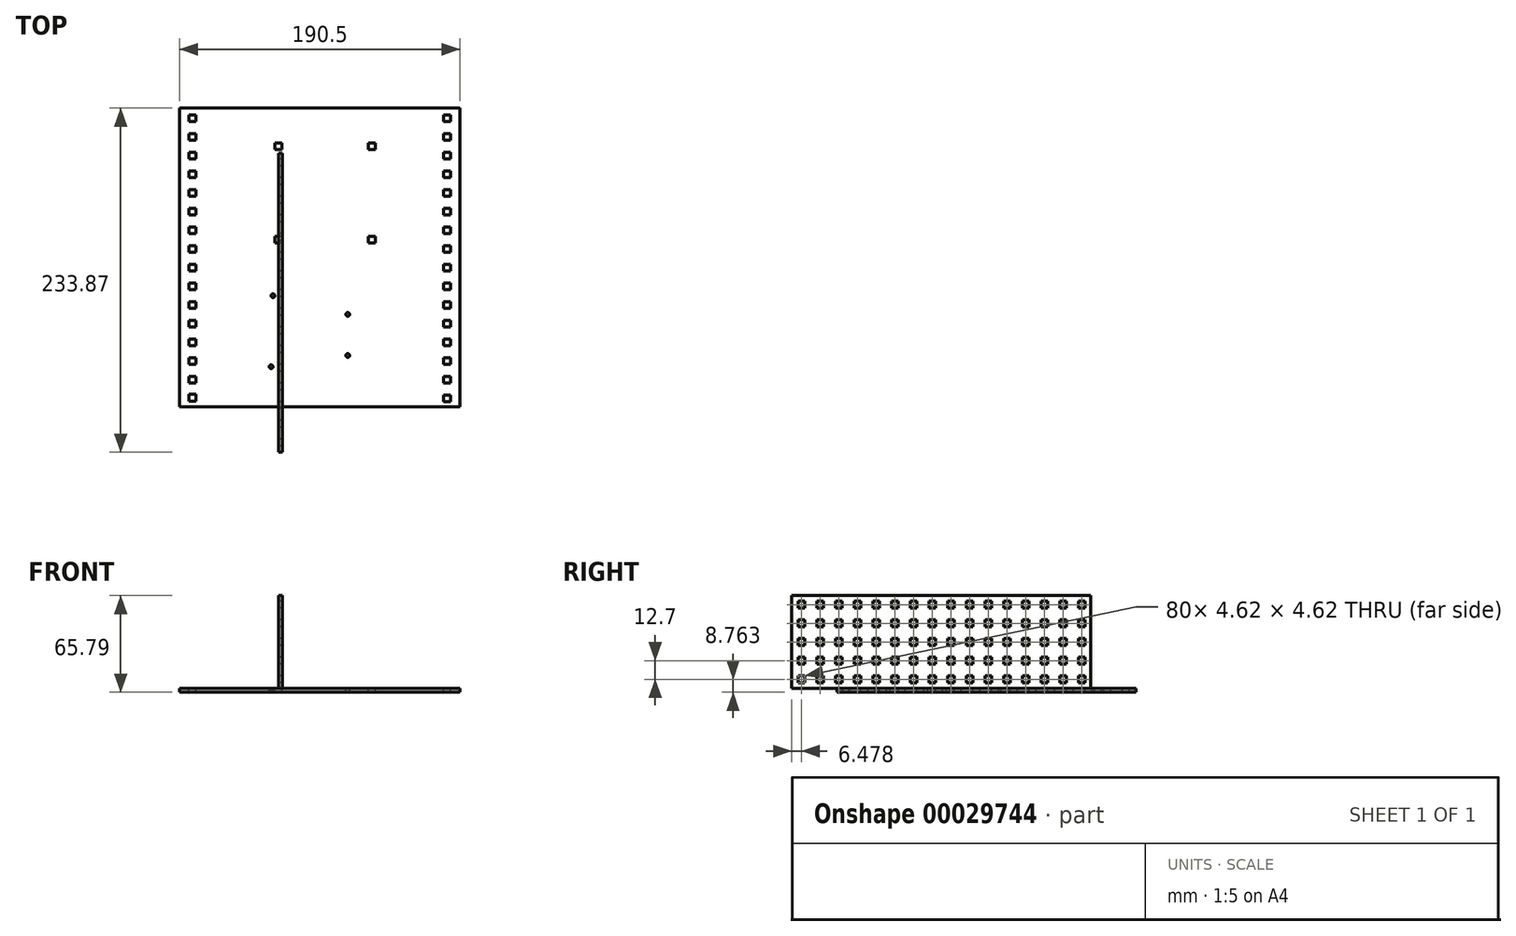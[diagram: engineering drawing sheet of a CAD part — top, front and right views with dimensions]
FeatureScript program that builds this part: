
annotation { "Feature Type Name" : "Feature", "Feature Type Description" : "" }
export const myFeature = defineFeature(function(context is Context, id is Id, definition is map)
    precondition{}
    {
        {
            var Q0;
            Q0=qCreatedBy(makeId("Top.planeOp"),FACE);
            var sketch = newSketch(context, id + "F0", { "sketchPlane" : qUnion([Q0])});
            skLineSegment(sketch, "E0.bottom", {"start": v(116.86, 111.67) * mm, "end": v(112.2, 111.67) * mm});
            skLineSegment(sketch, "E0.top", {"start": v(116.86, 107.05) * mm, "end": v(112.2, 107.05) * mm});
            skLineSegment(sketch, "E0.left", {"start": v(116.86, 111.67) * mm, "end": v(116.86, 107.05) * mm});
            skLineSegment(sketch, "E0.right", {"start": v(112.2, 111.67) * mm, "end": v(112.2, 107.05) * mm});
            skLineSegment(sketch, "E1.0.1.0", {"start": v(116.83, 94.35) * mm, "end": v(112.2, 94.35) * mm});
            skLineSegment(sketch, "E1.0.1.1", {"start": v(116.83, 98.97) * mm, "end": v(116.83, 94.35) * mm});
            skLineSegment(sketch, "E1.0.1.2", {"start": v(112.2, 98.97) * mm, "end": v(112.2, 94.35) * mm});
            skLineSegment(sketch, "E1.0.1.3", {"start": v(116.83, 98.97) * mm, "end": v(112.2, 98.97) * mm});
            skLineSegment(sketch, "E1.0.2.0", {"start": v(116.83, 81.65) * mm, "end": v(112.2, 81.65) * mm});
            skLineSegment(sketch, "E1.0.2.1", {"start": v(116.83, 86.27) * mm, "end": v(116.83, 81.65) * mm});
            skLineSegment(sketch, "E1.0.2.2", {"start": v(112.2, 86.27) * mm, "end": v(112.2, 81.65) * mm});
            skLineSegment(sketch, "E1.0.2.3", {"start": v(116.83, 86.27) * mm, "end": v(112.2, 86.27) * mm});
            skLineSegment(sketch, "E1.0.3.0", {"start": v(116.83, 68.95) * mm, "end": v(112.2, 68.95) * mm});
            skLineSegment(sketch, "E1.0.3.1", {"start": v(116.83, 73.57) * mm, "end": v(116.83, 68.95) * mm});
            skLineSegment(sketch, "E1.0.3.2", {"start": v(112.2, 73.57) * mm, "end": v(112.2, 68.95) * mm});
            skLineSegment(sketch, "E1.0.3.3", {"start": v(116.83, 73.57) * mm, "end": v(112.2, 73.57) * mm});
            skLineSegment(sketch, "E1.0.4.0", {"start": v(116.83, 56.25) * mm, "end": v(112.2, 56.25) * mm});
            skLineSegment(sketch, "E1.0.4.1", {"start": v(116.83, 60.87) * mm, "end": v(116.83, 56.25) * mm});
            skLineSegment(sketch, "E1.0.4.2", {"start": v(112.2, 60.87) * mm, "end": v(112.2, 56.25) * mm});
            skLineSegment(sketch, "E1.0.4.3", {"start": v(116.83, 60.87) * mm, "end": v(112.2, 60.87) * mm});
            skLineSegment(sketch, "E1.0.5.0", {"start": v(116.83, 43.55) * mm, "end": v(112.2, 43.55) * mm});
            skLineSegment(sketch, "E1.0.5.1", {"start": v(116.83, 48.17) * mm, "end": v(116.83, 43.55) * mm});
            skLineSegment(sketch, "E1.0.5.2", {"start": v(112.2, 48.17) * mm, "end": v(112.2, 43.55) * mm});
            skLineSegment(sketch, "E1.0.5.3", {"start": v(116.83, 48.17) * mm, "end": v(112.2, 48.17) * mm});
            skLineSegment(sketch, "E1.0.6.0", {"start": v(116.83, 30.85) * mm, "end": v(112.2, 30.85) * mm});
            skLineSegment(sketch, "E1.0.6.1", {"start": v(116.83, 35.47) * mm, "end": v(116.83, 30.85) * mm});
            skLineSegment(sketch, "E1.0.6.2", {"start": v(112.2, 35.47) * mm, "end": v(112.2, 30.85) * mm});
            skLineSegment(sketch, "E1.0.6.3", {"start": v(116.83, 35.47) * mm, "end": v(112.2, 35.47) * mm});
            skLineSegment(sketch, "E1.0.7.0", {"start": v(116.83, 18.15) * mm, "end": v(112.2, 18.15) * mm});
            skLineSegment(sketch, "E1.0.7.1", {"start": v(116.83, 22.77) * mm, "end": v(116.83, 18.15) * mm});
            skLineSegment(sketch, "E1.0.7.2", {"start": v(112.2, 22.77) * mm, "end": v(112.2, 18.15) * mm});
            skLineSegment(sketch, "E1.0.7.3", {"start": v(116.83, 22.77) * mm, "end": v(112.2, 22.77) * mm});
            skLineSegment(sketch, "E1.0.8.0", {"start": v(116.83, 5.45) * mm, "end": v(112.2, 5.45) * mm});
            skLineSegment(sketch, "E1.0.8.1", {"start": v(116.83, 10.07) * mm, "end": v(116.83, 5.45) * mm});
            skLineSegment(sketch, "E1.0.8.2", {"start": v(112.2, 10.07) * mm, "end": v(112.2, 5.45) * mm});
            skLineSegment(sketch, "E1.0.8.3", {"start": v(116.83, 10.07) * mm, "end": v(112.2, 10.07) * mm});
            skLineSegment(sketch, "E1.0.9.0", {"start": v(116.83, -7.25) * mm, "end": v(112.2, -7.25) * mm});
            skLineSegment(sketch, "E1.0.9.1", {"start": v(116.83, -2.63) * mm, "end": v(116.83, -7.25) * mm});
            skLineSegment(sketch, "E1.0.9.2", {"start": v(112.2, -2.63) * mm, "end": v(112.2, -7.25) * mm});
            skLineSegment(sketch, "E1.0.9.3", {"start": v(116.83, -2.63) * mm, "end": v(112.2, -2.63) * mm});
            skLineSegment(sketch, "E1.0.10.0", {"start": v(116.83, -19.95) * mm, "end": v(112.2, -19.95) * mm});
            skLineSegment(sketch, "E1.0.10.1", {"start": v(116.83, -15.33) * mm, "end": v(116.83, -19.95) * mm});
            skLineSegment(sketch, "E1.0.10.2", {"start": v(112.2, -15.33) * mm, "end": v(112.2, -19.95) * mm});
            skLineSegment(sketch, "E1.0.10.3", {"start": v(116.83, -15.33) * mm, "end": v(112.2, -15.33) * mm});
            skLineSegment(sketch, "E2.bottom", {"start": v(-60.74, 111.67) * mm, "end": v(-56.1, 111.67) * mm});
            skLineSegment(sketch, "E2.top", {"start": v(-60.74, 107.05) * mm, "end": v(-56.1, 107.05) * mm});
            skLineSegment(sketch, "E2.left", {"start": v(-60.74, 111.67) * mm, "end": v(-60.74, 107.05) * mm});
            skLineSegment(sketch, "E2.right", {"start": v(-56.1, 111.67) * mm, "end": v(-56.1, 107.05) * mm});
            skLineSegment(sketch, "E3.0.1.0", {"start": v(-56.1, 98.97) * mm, "end": v(-56.1, 94.35) * mm});
            skLineSegment(sketch, "E3.0.1.1", {"start": v(-60.72, 94.35) * mm, "end": v(-56.1, 94.35) * mm});
            skLineSegment(sketch, "E3.0.1.2", {"start": v(-60.72, 98.97) * mm, "end": v(-60.72, 94.35) * mm});
            skLineSegment(sketch, "E3.0.1.3", {"start": v(-60.72, 98.97) * mm, "end": v(-56.1, 98.97) * mm});
            skLineSegment(sketch, "E3.0.2.0", {"start": v(-56.1, 86.27) * mm, "end": v(-56.1, 81.65) * mm});
            skLineSegment(sketch, "E3.0.2.1", {"start": v(-60.72, 81.65) * mm, "end": v(-56.1, 81.65) * mm});
            skLineSegment(sketch, "E3.0.2.2", {"start": v(-60.72, 86.27) * mm, "end": v(-60.72, 81.65) * mm});
            skLineSegment(sketch, "E3.0.2.3", {"start": v(-60.72, 86.27) * mm, "end": v(-56.1, 86.27) * mm});
            skLineSegment(sketch, "E3.0.3.0", {"start": v(-56.1, 73.57) * mm, "end": v(-56.1, 68.95) * mm});
            skLineSegment(sketch, "E3.0.3.1", {"start": v(-60.72, 68.95) * mm, "end": v(-56.1, 68.95) * mm});
            skLineSegment(sketch, "E3.0.3.2", {"start": v(-60.72, 73.57) * mm, "end": v(-60.72, 68.95) * mm});
            skLineSegment(sketch, "E3.0.3.3", {"start": v(-60.72, 73.57) * mm, "end": v(-56.1, 73.57) * mm});
            skLineSegment(sketch, "E3.0.4.0", {"start": v(-56.1, 60.87) * mm, "end": v(-56.1, 56.25) * mm});
            skLineSegment(sketch, "E3.0.4.1", {"start": v(-60.72, 56.25) * mm, "end": v(-56.1, 56.25) * mm});
            skLineSegment(sketch, "E3.0.4.2", {"start": v(-60.72, 60.87) * mm, "end": v(-60.72, 56.25) * mm});
            skLineSegment(sketch, "E3.0.4.3", {"start": v(-60.72, 60.87) * mm, "end": v(-56.1, 60.87) * mm});
            skLineSegment(sketch, "E3.0.5.0", {"start": v(-56.1, 48.17) * mm, "end": v(-56.1, 43.55) * mm});
            skLineSegment(sketch, "E3.0.5.1", {"start": v(-60.72, 43.55) * mm, "end": v(-56.1, 43.55) * mm});
            skLineSegment(sketch, "E3.0.5.2", {"start": v(-60.72, 48.17) * mm, "end": v(-60.72, 43.55) * mm});
            skLineSegment(sketch, "E3.0.5.3", {"start": v(-60.72, 48.17) * mm, "end": v(-56.1, 48.17) * mm});
            skLineSegment(sketch, "E3.0.6.0", {"start": v(-56.1, 35.47) * mm, "end": v(-56.1, 30.85) * mm});
            skLineSegment(sketch, "E3.0.6.1", {"start": v(-60.72, 30.85) * mm, "end": v(-56.1, 30.85) * mm});
            skLineSegment(sketch, "E3.0.6.2", {"start": v(-60.72, 35.47) * mm, "end": v(-60.72, 30.85) * mm});
            skLineSegment(sketch, "E3.0.6.3", {"start": v(-60.72, 35.47) * mm, "end": v(-56.1, 35.47) * mm});
            skLineSegment(sketch, "E3.0.7.0", {"start": v(-56.1, 22.77) * mm, "end": v(-56.1, 18.15) * mm});
            skLineSegment(sketch, "E3.0.7.1", {"start": v(-60.72, 18.15) * mm, "end": v(-56.1, 18.15) * mm});
            skLineSegment(sketch, "E3.0.7.2", {"start": v(-60.72, 22.77) * mm, "end": v(-60.72, 18.15) * mm});
            skLineSegment(sketch, "E3.0.7.3", {"start": v(-60.72, 22.77) * mm, "end": v(-56.1, 22.77) * mm});
            skLineSegment(sketch, "E3.0.8.0", {"start": v(-56.1, 10.07) * mm, "end": v(-56.1, 5.45) * mm});
            skLineSegment(sketch, "E3.0.8.1", {"start": v(-60.72, 5.45) * mm, "end": v(-56.1, 5.45) * mm});
            skLineSegment(sketch, "E3.0.8.2", {"start": v(-60.72, 10.07) * mm, "end": v(-60.72, 5.45) * mm});
            skLineSegment(sketch, "E3.0.8.3", {"start": v(-60.72, 10.07) * mm, "end": v(-56.1, 10.07) * mm});
            skLineSegment(sketch, "E3.0.9.0", {"start": v(-56.1, -2.63) * mm, "end": v(-56.1, -7.25) * mm});
            skLineSegment(sketch, "E3.0.9.1", {"start": v(-60.72, -7.25) * mm, "end": v(-56.1, -7.25) * mm});
            skLineSegment(sketch, "E3.0.9.2", {"start": v(-60.72, -2.63) * mm, "end": v(-60.72, -7.25) * mm});
            skLineSegment(sketch, "E3.0.9.3", {"start": v(-60.72, -2.63) * mm, "end": v(-56.1, -2.63) * mm});
            skLineSegment(sketch, "E3.0.10.0", {"start": v(-56.1, -15.33) * mm, "end": v(-56.1, -19.95) * mm});
            skLineSegment(sketch, "E3.0.10.1", {"start": v(-60.72, -19.95) * mm, "end": v(-56.1, -19.95) * mm});
            skLineSegment(sketch, "E3.0.10.2", {"start": v(-60.72, -15.33) * mm, "end": v(-60.72, -19.95) * mm});
            skLineSegment(sketch, "E3.0.10.3", {"start": v(-60.72, -15.33) * mm, "end": v(-56.1, -15.33) * mm});
            skLineSegment(sketch, "E4", {"start": v(-67.2, 141.63) * mm, "end": v(-67.2, -61.57) * mm});
            skLineSegment(sketch, "E5.0.0.11", {"start": v(-56.1, -28.03) * mm, "end": v(-56.1, -32.65) * mm});
            skLineSegment(sketch, "E5.3.0.11", {"start": v(-60.72, -32.65) * mm, "end": v(-56.1, -32.65) * mm});
            skLineSegment(sketch, "E5.6.0.11", {"start": v(-60.72, -28.03) * mm, "end": v(-60.72, -32.65) * mm});
            skLineSegment(sketch, "E5.9.0.11", {"start": v(-60.72, -28.03) * mm, "end": v(-56.1, -28.03) * mm});
            skLineSegment(sketch, "E5.0.0.12", {"start": v(-56.1, -40.73) * mm, "end": v(-56.1, -45.35) * mm});
            skLineSegment(sketch, "E5.3.0.12", {"start": v(-60.72, -45.35) * mm, "end": v(-56.1, -45.35) * mm});
            skLineSegment(sketch, "E5.6.0.12", {"start": v(-60.72, -40.73) * mm, "end": v(-60.72, -45.35) * mm});
            skLineSegment(sketch, "E5.9.0.12", {"start": v(-60.72, -40.73) * mm, "end": v(-56.1, -40.73) * mm});
            skLineSegment(sketch, "E5.0.0.13", {"start": v(-56.07, -52.9) * mm, "end": v(-56.07, -57.53) * mm});
            skLineSegment(sketch, "E5.3.0.13", {"start": v(-60.72, -57.53) * mm, "end": v(-56.07, -57.53) * mm});
            skLineSegment(sketch, "E5.6.0.13", {"start": v(-60.72, -52.9) * mm, "end": v(-60.72, -57.53) * mm});
            skLineSegment(sketch, "E5.9.0.13", {"start": v(-60.72, -52.9) * mm, "end": v(-56.07, -52.9) * mm});
            skLineSegment(sketch, "E6.0.0.11", {"start": v(116.83, -32.65) * mm, "end": v(112.2, -32.65) * mm});
            skLineSegment(sketch, "E6.3.0.11", {"start": v(116.83, -28.03) * mm, "end": v(116.83, -32.65) * mm});
            skLineSegment(sketch, "E6.6.0.11", {"start": v(112.2, -28.03) * mm, "end": v(112.2, -32.65) * mm});
            skLineSegment(sketch, "E6.9.0.11", {"start": v(116.83, -28.03) * mm, "end": v(112.2, -28.03) * mm});
            skLineSegment(sketch, "E6.0.0.12", {"start": v(116.83, -45.35) * mm, "end": v(112.2, -45.35) * mm});
            skLineSegment(sketch, "E6.3.0.12", {"start": v(116.83, -40.73) * mm, "end": v(116.83, -45.35) * mm});
            skLineSegment(sketch, "E6.6.0.12", {"start": v(112.2, -40.73) * mm, "end": v(112.2, -45.35) * mm});
            skLineSegment(sketch, "E6.9.0.12", {"start": v(116.83, -40.73) * mm, "end": v(112.2, -40.73) * mm});
            skLineSegment(sketch, "E6.0.0.13", {"start": v(116.83, -58.05) * mm, "end": v(112.2, -58.05) * mm});
            skLineSegment(sketch, "E6.3.0.13", {"start": v(116.83, -53.43) * mm, "end": v(116.83, -58.05) * mm});
            skLineSegment(sketch, "E6.6.0.13", {"start": v(112.2, -53.43) * mm, "end": v(112.2, -58.05) * mm});
            skLineSegment(sketch, "E6.9.0.13", {"start": v(116.83, -53.43) * mm, "end": v(112.2, -53.43) * mm});
            skCircle(sketch, "E7", {"center": v(-3.7, 14.1) * mm, "radius": 1.27 * mm});
            skCircle(sketch, "E8", {"center": v(47.1, 1.4) * mm, "radius": 1.27 * mm});
            skCircle(sketch, "E9", {"center": v(47.1, -26.53) * mm, "radius": 1.27 * mm});
            skCircle(sketch, "E10", {"center": v(-4.96, -34.15) * mm, "radius": 1.27 * mm});
            skLineSegment(sketch, "E11", {"start": v(-60.74, 124.37) * mm, "end": v(-56.1, 124.37) * mm});
            skLineSegment(sketch, "E12", {"start": v(-56.1, 124.37) * mm, "end": v(-56.1, 119.72) * mm});
            skLineSegment(sketch, "E13", {"start": v(-56.1, 119.72) * mm, "end": v(-60.74, 119.72) * mm});
            skLineSegment(sketch, "E14", {"start": v(-56.1, 137.07) * mm, "end": v(-56.1, 132.42) * mm});
            skLineSegment(sketch, "E15", {"start": v(-56.1, 132.42) * mm, "end": v(-60.74, 132.42) * mm});
            skLineSegment(sketch, "E16", {"start": v(-60.74, 124.37) * mm, "end": v(-60.74, 119.72) * mm});
            skLineSegment(sketch, "E17", {"start": v(112.2, 124.37) * mm, "end": v(116.86, 124.37) * mm});
            skLineSegment(sketch, "E18", {"start": v(116.86, 124.37) * mm, "end": v(116.86, 119.72) * mm});
            skLineSegment(sketch, "E19", {"start": v(112.2, 137.07) * mm, "end": v(116.86, 137.07) * mm});
            skLineSegment(sketch, "E20", {"start": v(116.86, 137.07) * mm, "end": v(116.86, 132.42) * mm});
            skLineSegment(sketch, "E21", {"start": v(116.86, 132.42) * mm, "end": v(112.2, 132.42) * mm});
            skLineSegment(sketch, "E22", {"start": v(116.86, 119.72) * mm, "end": v(112.2, 119.72) * mm});
            skLineSegment(sketch, "E23", {"start": v(112.2, 119.72) * mm, "end": v(112.2, 124.37) * mm});
            skLineSegment(sketch, "E24", {"start": v(112.2, 137.07) * mm, "end": v(112.2, 132.42) * mm});
            skLineSegment(sketch, "E25.rect.bottom", {"start": v(2.32, 113.39) * mm, "end": v(-2.32, 113.39) * mm});
            skLineSegment(sketch, "E25.rect.top", {"start": v(2.32, 118.03) * mm, "end": v(-2.32, 118.03) * mm});
            skLineSegment(sketch, "E25.rect.left", {"start": v(2.32, 113.39) * mm, "end": v(2.32, 118.03) * mm});
            skLineSegment(sketch, "E25.rect.right", {"start": v(-2.32, 113.39) * mm, "end": v(-2.32, 118.03) * mm});
            skPoint(sketch, "E25.rect.middle", {"position": v(0, 115.7) * mm});
            skLineSegment(sketch, "E26.rect.bottom", {"start": v(61.18, 113.39) * mm, "end": v(65.82, 113.39) * mm});
            skLineSegment(sketch, "E26.rect.top", {"start": v(61.18, 118.03) * mm, "end": v(65.82, 118.03) * mm});
            skLineSegment(sketch, "E26.rect.left", {"start": v(61.18, 113.39) * mm, "end": v(61.18, 118.03) * mm});
            skLineSegment(sketch, "E26.rect.right", {"start": v(65.82, 113.39) * mm, "end": v(65.82, 118.03) * mm});
            skPoint(sketch, "E26.rect.middle", {"position": v(63.5, 115.7) * mm});
            skPoint(sketch, "E27.endSnap0", {"position": v(0, 113.39) * mm});
            skLineSegment(sketch, "E28.rect.bottom", {"start": v(2.32, 49.89) * mm, "end": v(-2.32, 49.89) * mm});
            skLineSegment(sketch, "E28.rect.top", {"start": v(2.32, 54.53) * mm, "end": v(-2.32, 54.53) * mm});
            skLineSegment(sketch, "E28.rect.left", {"start": v(2.32, 49.89) * mm, "end": v(2.32, 54.53) * mm});
            skLineSegment(sketch, "E28.rect.right", {"start": v(-2.32, 49.89) * mm, "end": v(-2.32, 54.53) * mm});
            skPoint(sketch, "E28.rect.middle", {"position": v(0, 52.2) * mm});
            skLineSegment(sketch, "E29.rect.bottom", {"start": v(65.82, 49.89) * mm, "end": v(61.18, 49.89) * mm});
            skLineSegment(sketch, "E29.rect.top", {"start": v(65.82, 54.53) * mm, "end": v(61.18, 54.53) * mm});
            skLineSegment(sketch, "E29.rect.left", {"start": v(65.82, 49.89) * mm, "end": v(65.82, 54.53) * mm});
            skLineSegment(sketch, "E29.rect.right", {"start": v(61.18, 49.89) * mm, "end": v(61.18, 54.53) * mm});
            skPoint(sketch, "E29.rect.middle", {"position": v(63.5, 52.2) * mm});
            skLineSegment(sketch, "E30", {"start": v(-67.2, -61.57) * mm, "end": v(123.3, -61.57) * mm});
            skLineSegment(sketch, "E31", {"start": v(123.3, 141.63) * mm, "end": v(123.3, -61.57) * mm});
            skLineSegment(sketch, "E32", {"start": v(-67.2, 141.63) * mm, "end": v(123.3, 141.63) * mm});
            skLineSegment(sketch, "E33", {"start": v(-56.1, 137.07) * mm, "end": v(-60.74, 137.07) * mm});
            skLineSegment(sketch, "E34", {"start": v(-60.74, 137.07) * mm, "end": v(-60.74, 132.42) * mm});
            skSolve(sketch);
        }
        {
            var Q0;
            Q0=qCreatedBy(makeId("Right.planeOp"),FACE);
            var sketch = newSketch(context, id + "F1", { "sketchPlane" : qUnion([Q0])});
            skLineSegment(sketch, "E35", {"start": v(110.96, 0) * mm, "end": v(110.96, 63.25) * mm});
            skLineSegment(sketch, "E36", {"start": v(-92.24, 63.25) * mm, "end": v(-92.24, 0) * mm});
            skLineSegment(sketch, "E37", {"start": v(110.96, 63.25) * mm, "end": v(-92.24, 63.25) * mm});
            skLineSegment(sketch, "E38", {"start": v(110.96, 0) * mm, "end": v(-92.24, 0) * mm});
            skLineSegment(sketch, "E39.bottom", {"start": v(107.05, 59.33) * mm, "end": v(102.43, 59.33) * mm});
            skLineSegment(sketch, "E39.top", {"start": v(107.05, 54.71) * mm, "end": v(102.43, 54.71) * mm});
            skLineSegment(sketch, "E39.left", {"start": v(107.05, 59.33) * mm, "end": v(107.05, 54.71) * mm});
            skLineSegment(sketch, "E39.right", {"start": v(102.43, 59.33) * mm, "end": v(102.43, 54.71) * mm});
            skLineSegment(sketch, "E40.0.1.0", {"start": v(107.05, 42.01) * mm, "end": v(102.43, 42.01) * mm});
            skLineSegment(sketch, "E40.0.1.1", {"start": v(107.05, 46.63) * mm, "end": v(107.05, 42.01) * mm});
            skLineSegment(sketch, "E40.0.1.2", {"start": v(107.05, 46.63) * mm, "end": v(102.43, 46.63) * mm});
            skLineSegment(sketch, "E40.0.1.3", {"start": v(102.43, 46.63) * mm, "end": v(102.43, 42.01) * mm});
            skLineSegment(sketch, "E40.0.2.0", {"start": v(107.05, 29.31) * mm, "end": v(102.43, 29.31) * mm});
            skLineSegment(sketch, "E40.0.2.1", {"start": v(107.05, 33.93) * mm, "end": v(107.05, 29.31) * mm});
            skLineSegment(sketch, "E40.0.2.2", {"start": v(107.05, 33.93) * mm, "end": v(102.43, 33.93) * mm});
            skLineSegment(sketch, "E40.0.2.3", {"start": v(102.43, 33.93) * mm, "end": v(102.43, 29.31) * mm});
            skLineSegment(sketch, "E40.0.3.0", {"start": v(107.05, 16.61) * mm, "end": v(102.43, 16.61) * mm});
            skLineSegment(sketch, "E40.0.3.1", {"start": v(107.05, 21.23) * mm, "end": v(107.05, 16.61) * mm});
            skLineSegment(sketch, "E40.0.3.2", {"start": v(107.05, 21.23) * mm, "end": v(102.43, 21.23) * mm});
            skLineSegment(sketch, "E40.0.3.3", {"start": v(102.43, 21.23) * mm, "end": v(102.43, 16.61) * mm});
            skLineSegment(sketch, "E40.0.4.0", {"start": v(107.05, 3.91) * mm, "end": v(102.43, 3.91) * mm});
            skLineSegment(sketch, "E40.0.4.1", {"start": v(107.05, 8.53) * mm, "end": v(107.05, 3.91) * mm});
            skLineSegment(sketch, "E40.0.4.2", {"start": v(107.05, 8.53) * mm, "end": v(102.43, 8.53) * mm});
            skLineSegment(sketch, "E40.0.4.3", {"start": v(102.43, 8.53) * mm, "end": v(102.43, 3.91) * mm});
            skLineSegment(sketch, "E40.1.0.0", {"start": v(94.35, 54.71) * mm, "end": v(89.73, 54.71) * mm});
            skLineSegment(sketch, "E40.1.0.1", {"start": v(94.35, 59.33) * mm, "end": v(94.35, 54.71) * mm});
            skLineSegment(sketch, "E40.1.0.2", {"start": v(94.35, 59.33) * mm, "end": v(89.73, 59.33) * mm});
            skLineSegment(sketch, "E40.1.0.3", {"start": v(89.73, 59.33) * mm, "end": v(89.73, 54.71) * mm});
            skLineSegment(sketch, "E40.1.1.0", {"start": v(94.35, 42.01) * mm, "end": v(89.73, 42.01) * mm});
            skLineSegment(sketch, "E40.1.1.1", {"start": v(94.35, 46.63) * mm, "end": v(94.35, 42.01) * mm});
            skLineSegment(sketch, "E40.1.1.2", {"start": v(94.35, 46.63) * mm, "end": v(89.73, 46.63) * mm});
            skLineSegment(sketch, "E40.1.1.3", {"start": v(89.73, 46.63) * mm, "end": v(89.73, 42.01) * mm});
            skLineSegment(sketch, "E40.1.2.0", {"start": v(94.35, 29.31) * mm, "end": v(89.73, 29.31) * mm});
            skLineSegment(sketch, "E40.1.2.1", {"start": v(94.35, 33.93) * mm, "end": v(94.35, 29.31) * mm});
            skLineSegment(sketch, "E40.1.2.2", {"start": v(94.35, 33.93) * mm, "end": v(89.73, 33.93) * mm});
            skLineSegment(sketch, "E40.1.2.3", {"start": v(89.73, 33.93) * mm, "end": v(89.73, 29.31) * mm});
            skLineSegment(sketch, "E40.1.3.0", {"start": v(94.35, 16.61) * mm, "end": v(89.73, 16.61) * mm});
            skLineSegment(sketch, "E40.1.3.1", {"start": v(94.35, 21.23) * mm, "end": v(94.35, 16.61) * mm});
            skLineSegment(sketch, "E40.1.3.2", {"start": v(94.35, 21.23) * mm, "end": v(89.73, 21.23) * mm});
            skLineSegment(sketch, "E40.1.3.3", {"start": v(89.73, 21.23) * mm, "end": v(89.73, 16.61) * mm});
            skLineSegment(sketch, "E40.1.4.0", {"start": v(94.35, 3.91) * mm, "end": v(89.73, 3.91) * mm});
            skLineSegment(sketch, "E40.1.4.1", {"start": v(94.35, 8.53) * mm, "end": v(94.35, 3.91) * mm});
            skLineSegment(sketch, "E40.1.4.2", {"start": v(94.35, 8.53) * mm, "end": v(89.73, 8.53) * mm});
            skLineSegment(sketch, "E40.1.4.3", {"start": v(89.73, 8.53) * mm, "end": v(89.73, 3.91) * mm});
            skLineSegment(sketch, "E40.2.0.0", {"start": v(81.65, 54.71) * mm, "end": v(77.03, 54.71) * mm});
            skLineSegment(sketch, "E40.2.0.1", {"start": v(81.65, 59.33) * mm, "end": v(81.65, 54.71) * mm});
            skLineSegment(sketch, "E40.2.0.2", {"start": v(81.65, 59.33) * mm, "end": v(77.03, 59.33) * mm});
            skLineSegment(sketch, "E40.2.0.3", {"start": v(77.03, 59.33) * mm, "end": v(77.03, 54.71) * mm});
            skLineSegment(sketch, "E40.2.1.0", {"start": v(81.65, 42.01) * mm, "end": v(77.03, 42.01) * mm});
            skLineSegment(sketch, "E40.2.1.1", {"start": v(81.65, 46.63) * mm, "end": v(81.65, 42.01) * mm});
            skLineSegment(sketch, "E40.2.1.2", {"start": v(81.65, 46.63) * mm, "end": v(77.03, 46.63) * mm});
            skLineSegment(sketch, "E40.2.1.3", {"start": v(77.03, 46.63) * mm, "end": v(77.03, 42.01) * mm});
            skLineSegment(sketch, "E40.2.2.0", {"start": v(81.65, 29.31) * mm, "end": v(77.03, 29.31) * mm});
            skLineSegment(sketch, "E40.2.2.1", {"start": v(81.65, 33.93) * mm, "end": v(81.65, 29.31) * mm});
            skLineSegment(sketch, "E40.2.2.2", {"start": v(81.65, 33.93) * mm, "end": v(77.03, 33.93) * mm});
            skLineSegment(sketch, "E40.2.2.3", {"start": v(77.03, 33.93) * mm, "end": v(77.03, 29.31) * mm});
            skLineSegment(sketch, "E40.2.3.0", {"start": v(81.65, 16.61) * mm, "end": v(77.03, 16.61) * mm});
            skLineSegment(sketch, "E40.2.3.1", {"start": v(81.65, 21.23) * mm, "end": v(81.65, 16.61) * mm});
            skLineSegment(sketch, "E40.2.3.2", {"start": v(81.65, 21.23) * mm, "end": v(77.03, 21.23) * mm});
            skLineSegment(sketch, "E40.2.3.3", {"start": v(77.03, 21.23) * mm, "end": v(77.03, 16.61) * mm});
            skLineSegment(sketch, "E40.2.4.0", {"start": v(81.65, 3.91) * mm, "end": v(77.03, 3.91) * mm});
            skLineSegment(sketch, "E40.2.4.1", {"start": v(81.65, 8.53) * mm, "end": v(81.65, 3.91) * mm});
            skLineSegment(sketch, "E40.2.4.2", {"start": v(81.65, 8.53) * mm, "end": v(77.03, 8.53) * mm});
            skLineSegment(sketch, "E40.2.4.3", {"start": v(77.03, 8.53) * mm, "end": v(77.03, 3.91) * mm});
            skLineSegment(sketch, "E40.3.0.0", {"start": v(68.95, 54.71) * mm, "end": v(64.33, 54.71) * mm});
            skLineSegment(sketch, "E40.3.0.1", {"start": v(68.95, 59.33) * mm, "end": v(68.95, 54.71) * mm});
            skLineSegment(sketch, "E40.3.0.2", {"start": v(68.95, 59.33) * mm, "end": v(64.33, 59.33) * mm});
            skLineSegment(sketch, "E40.3.0.3", {"start": v(64.33, 59.33) * mm, "end": v(64.33, 54.71) * mm});
            skLineSegment(sketch, "E40.3.1.0", {"start": v(68.95, 42.01) * mm, "end": v(64.33, 42.01) * mm});
            skLineSegment(sketch, "E40.3.1.1", {"start": v(68.95, 46.63) * mm, "end": v(68.95, 42.01) * mm});
            skLineSegment(sketch, "E40.3.1.2", {"start": v(68.95, 46.63) * mm, "end": v(64.33, 46.63) * mm});
            skLineSegment(sketch, "E40.3.1.3", {"start": v(64.33, 46.63) * mm, "end": v(64.33, 42.01) * mm});
            skLineSegment(sketch, "E40.3.2.0", {"start": v(68.95, 29.31) * mm, "end": v(64.33, 29.31) * mm});
            skLineSegment(sketch, "E40.3.2.1", {"start": v(68.95, 33.93) * mm, "end": v(68.95, 29.31) * mm});
            skLineSegment(sketch, "E40.3.2.2", {"start": v(68.95, 33.93) * mm, "end": v(64.33, 33.93) * mm});
            skLineSegment(sketch, "E40.3.2.3", {"start": v(64.33, 33.93) * mm, "end": v(64.33, 29.31) * mm});
            skLineSegment(sketch, "E40.3.3.0", {"start": v(68.95, 16.61) * mm, "end": v(64.33, 16.61) * mm});
            skLineSegment(sketch, "E40.3.3.1", {"start": v(68.95, 21.23) * mm, "end": v(68.95, 16.61) * mm});
            skLineSegment(sketch, "E40.3.3.2", {"start": v(68.95, 21.23) * mm, "end": v(64.33, 21.23) * mm});
            skLineSegment(sketch, "E40.3.3.3", {"start": v(64.33, 21.23) * mm, "end": v(64.33, 16.61) * mm});
            skLineSegment(sketch, "E40.3.4.0", {"start": v(68.95, 3.91) * mm, "end": v(64.33, 3.91) * mm});
            skLineSegment(sketch, "E40.3.4.1", {"start": v(68.95, 8.53) * mm, "end": v(68.95, 3.91) * mm});
            skLineSegment(sketch, "E40.3.4.2", {"start": v(68.95, 8.53) * mm, "end": v(64.33, 8.53) * mm});
            skLineSegment(sketch, "E40.3.4.3", {"start": v(64.33, 8.53) * mm, "end": v(64.33, 3.91) * mm});
            skLineSegment(sketch, "E40.4.0.0", {"start": v(56.25, 54.71) * mm, "end": v(51.63, 54.71) * mm});
            skLineSegment(sketch, "E40.4.0.1", {"start": v(56.25, 59.33) * mm, "end": v(56.25, 54.71) * mm});
            skLineSegment(sketch, "E40.4.0.2", {"start": v(56.25, 59.33) * mm, "end": v(51.63, 59.33) * mm});
            skLineSegment(sketch, "E40.4.0.3", {"start": v(51.63, 59.33) * mm, "end": v(51.63, 54.71) * mm});
            skLineSegment(sketch, "E40.4.1.0", {"start": v(56.25, 42.01) * mm, "end": v(51.63, 42.01) * mm});
            skLineSegment(sketch, "E40.4.1.1", {"start": v(56.25, 46.63) * mm, "end": v(56.25, 42.01) * mm});
            skLineSegment(sketch, "E40.4.1.2", {"start": v(56.25, 46.63) * mm, "end": v(51.63, 46.63) * mm});
            skLineSegment(sketch, "E40.4.1.3", {"start": v(51.63, 46.63) * mm, "end": v(51.63, 42.01) * mm});
            skLineSegment(sketch, "E40.4.2.0", {"start": v(56.25, 29.31) * mm, "end": v(51.63, 29.31) * mm});
            skLineSegment(sketch, "E40.4.2.1", {"start": v(56.25, 33.93) * mm, "end": v(56.25, 29.31) * mm});
            skLineSegment(sketch, "E40.4.2.2", {"start": v(56.25, 33.93) * mm, "end": v(51.63, 33.93) * mm});
            skLineSegment(sketch, "E40.4.2.3", {"start": v(51.63, 33.93) * mm, "end": v(51.63, 29.31) * mm});
            skLineSegment(sketch, "E40.4.3.0", {"start": v(56.25, 16.61) * mm, "end": v(51.63, 16.61) * mm});
            skLineSegment(sketch, "E40.4.3.1", {"start": v(56.25, 21.23) * mm, "end": v(56.25, 16.61) * mm});
            skLineSegment(sketch, "E40.4.3.2", {"start": v(56.25, 21.23) * mm, "end": v(51.63, 21.23) * mm});
            skLineSegment(sketch, "E40.4.3.3", {"start": v(51.63, 21.23) * mm, "end": v(51.63, 16.61) * mm});
            skLineSegment(sketch, "E40.4.4.0", {"start": v(56.25, 3.91) * mm, "end": v(51.63, 3.91) * mm});
            skLineSegment(sketch, "E40.4.4.1", {"start": v(56.25, 8.53) * mm, "end": v(56.25, 3.91) * mm});
            skLineSegment(sketch, "E40.4.4.2", {"start": v(56.25, 8.53) * mm, "end": v(51.63, 8.53) * mm});
            skLineSegment(sketch, "E40.4.4.3", {"start": v(51.63, 8.53) * mm, "end": v(51.63, 3.91) * mm});
            skLineSegment(sketch, "E40.5.0.0", {"start": v(43.55, 54.71) * mm, "end": v(38.93, 54.71) * mm});
            skLineSegment(sketch, "E40.5.0.1", {"start": v(43.55, 59.33) * mm, "end": v(43.55, 54.71) * mm});
            skLineSegment(sketch, "E40.5.0.2", {"start": v(43.55, 59.33) * mm, "end": v(38.93, 59.33) * mm});
            skLineSegment(sketch, "E40.5.0.3", {"start": v(38.93, 59.33) * mm, "end": v(38.93, 54.71) * mm});
            skLineSegment(sketch, "E40.5.1.0", {"start": v(43.55, 42.01) * mm, "end": v(38.93, 42.01) * mm});
            skLineSegment(sketch, "E40.5.1.1", {"start": v(43.55, 46.63) * mm, "end": v(43.55, 42.01) * mm});
            skLineSegment(sketch, "E40.5.1.2", {"start": v(43.55, 46.63) * mm, "end": v(38.93, 46.63) * mm});
            skLineSegment(sketch, "E40.5.1.3", {"start": v(38.93, 46.63) * mm, "end": v(38.93, 42.01) * mm});
            skLineSegment(sketch, "E40.5.2.0", {"start": v(43.55, 29.31) * mm, "end": v(38.93, 29.31) * mm});
            skLineSegment(sketch, "E40.5.2.1", {"start": v(43.55, 33.93) * mm, "end": v(43.55, 29.31) * mm});
            skLineSegment(sketch, "E40.5.2.2", {"start": v(43.55, 33.93) * mm, "end": v(38.93, 33.93) * mm});
            skLineSegment(sketch, "E40.5.2.3", {"start": v(38.93, 33.93) * mm, "end": v(38.93, 29.31) * mm});
            skLineSegment(sketch, "E40.5.3.0", {"start": v(43.55, 16.61) * mm, "end": v(38.93, 16.61) * mm});
            skLineSegment(sketch, "E40.5.3.1", {"start": v(43.55, 21.23) * mm, "end": v(43.55, 16.61) * mm});
            skLineSegment(sketch, "E40.5.3.2", {"start": v(43.55, 21.23) * mm, "end": v(38.93, 21.23) * mm});
            skLineSegment(sketch, "E40.5.3.3", {"start": v(38.93, 21.23) * mm, "end": v(38.93, 16.61) * mm});
            skLineSegment(sketch, "E40.5.4.0", {"start": v(43.55, 3.91) * mm, "end": v(38.93, 3.91) * mm});
            skLineSegment(sketch, "E40.5.4.1", {"start": v(43.55, 8.53) * mm, "end": v(43.55, 3.91) * mm});
            skLineSegment(sketch, "E40.5.4.2", {"start": v(43.55, 8.53) * mm, "end": v(38.93, 8.53) * mm});
            skLineSegment(sketch, "E40.5.4.3", {"start": v(38.93, 8.53) * mm, "end": v(38.93, 3.91) * mm});
            skLineSegment(sketch, "E40.6.0.0", {"start": v(30.85, 54.71) * mm, "end": v(26.23, 54.71) * mm});
            skLineSegment(sketch, "E40.6.0.1", {"start": v(30.85, 59.33) * mm, "end": v(30.85, 54.71) * mm});
            skLineSegment(sketch, "E40.6.0.2", {"start": v(30.85, 59.33) * mm, "end": v(26.23, 59.33) * mm});
            skLineSegment(sketch, "E40.6.0.3", {"start": v(26.23, 59.33) * mm, "end": v(26.23, 54.71) * mm});
            skLineSegment(sketch, "E40.6.1.0", {"start": v(30.85, 42.01) * mm, "end": v(26.23, 42.01) * mm});
            skLineSegment(sketch, "E40.6.1.1", {"start": v(30.85, 46.63) * mm, "end": v(30.85, 42.01) * mm});
            skLineSegment(sketch, "E40.6.1.2", {"start": v(30.85, 46.63) * mm, "end": v(26.23, 46.63) * mm});
            skLineSegment(sketch, "E40.6.1.3", {"start": v(26.23, 46.63) * mm, "end": v(26.23, 42.01) * mm});
            skLineSegment(sketch, "E40.6.2.0", {"start": v(30.85, 29.31) * mm, "end": v(26.23, 29.31) * mm});
            skLineSegment(sketch, "E40.6.2.1", {"start": v(30.85, 33.93) * mm, "end": v(30.85, 29.31) * mm});
            skLineSegment(sketch, "E40.6.2.2", {"start": v(30.85, 33.93) * mm, "end": v(26.23, 33.93) * mm});
            skLineSegment(sketch, "E40.6.2.3", {"start": v(26.23, 33.93) * mm, "end": v(26.23, 29.31) * mm});
            skLineSegment(sketch, "E40.6.3.0", {"start": v(30.85, 16.61) * mm, "end": v(26.23, 16.61) * mm});
            skLineSegment(sketch, "E40.6.3.1", {"start": v(30.85, 21.23) * mm, "end": v(30.85, 16.61) * mm});
            skLineSegment(sketch, "E40.6.3.2", {"start": v(30.85, 21.23) * mm, "end": v(26.23, 21.23) * mm});
            skLineSegment(sketch, "E40.6.3.3", {"start": v(26.23, 21.23) * mm, "end": v(26.23, 16.61) * mm});
            skLineSegment(sketch, "E40.6.4.0", {"start": v(30.85, 3.91) * mm, "end": v(26.23, 3.91) * mm});
            skLineSegment(sketch, "E40.6.4.1", {"start": v(30.85, 8.53) * mm, "end": v(30.85, 3.91) * mm});
            skLineSegment(sketch, "E40.6.4.2", {"start": v(30.85, 8.53) * mm, "end": v(26.23, 8.53) * mm});
            skLineSegment(sketch, "E40.6.4.3", {"start": v(26.23, 8.53) * mm, "end": v(26.23, 3.91) * mm});
            skLineSegment(sketch, "E40.7.0.0", {"start": v(18.15, 54.71) * mm, "end": v(13.53, 54.71) * mm});
            skLineSegment(sketch, "E40.7.0.1", {"start": v(18.15, 59.33) * mm, "end": v(18.15, 54.71) * mm});
            skLineSegment(sketch, "E40.7.0.2", {"start": v(18.15, 59.33) * mm, "end": v(13.53, 59.33) * mm});
            skLineSegment(sketch, "E40.7.0.3", {"start": v(13.53, 59.33) * mm, "end": v(13.53, 54.71) * mm});
            skLineSegment(sketch, "E40.7.1.0", {"start": v(18.15, 42.01) * mm, "end": v(13.53, 42.01) * mm});
            skLineSegment(sketch, "E40.7.1.1", {"start": v(18.15, 46.63) * mm, "end": v(18.15, 42.01) * mm});
            skLineSegment(sketch, "E40.7.1.2", {"start": v(18.15, 46.63) * mm, "end": v(13.53, 46.63) * mm});
            skLineSegment(sketch, "E40.7.1.3", {"start": v(13.53, 46.63) * mm, "end": v(13.53, 42.01) * mm});
            skLineSegment(sketch, "E40.7.2.0", {"start": v(18.15, 29.31) * mm, "end": v(13.53, 29.31) * mm});
            skLineSegment(sketch, "E40.7.2.1", {"start": v(18.15, 33.93) * mm, "end": v(18.15, 29.31) * mm});
            skLineSegment(sketch, "E40.7.2.2", {"start": v(18.15, 33.93) * mm, "end": v(13.53, 33.93) * mm});
            skLineSegment(sketch, "E40.7.2.3", {"start": v(13.53, 33.93) * mm, "end": v(13.53, 29.31) * mm});
            skLineSegment(sketch, "E40.7.3.0", {"start": v(18.15, 16.61) * mm, "end": v(13.53, 16.61) * mm});
            skLineSegment(sketch, "E40.7.3.1", {"start": v(18.15, 21.23) * mm, "end": v(18.15, 16.61) * mm});
            skLineSegment(sketch, "E40.7.3.2", {"start": v(18.15, 21.23) * mm, "end": v(13.53, 21.23) * mm});
            skLineSegment(sketch, "E40.7.3.3", {"start": v(13.53, 21.23) * mm, "end": v(13.53, 16.61) * mm});
            skLineSegment(sketch, "E40.7.4.0", {"start": v(18.15, 3.91) * mm, "end": v(13.53, 3.91) * mm});
            skLineSegment(sketch, "E40.7.4.1", {"start": v(18.15, 8.53) * mm, "end": v(18.15, 3.91) * mm});
            skLineSegment(sketch, "E40.7.4.2", {"start": v(18.15, 8.53) * mm, "end": v(13.53, 8.53) * mm});
            skLineSegment(sketch, "E40.7.4.3", {"start": v(13.53, 8.53) * mm, "end": v(13.53, 3.91) * mm});
            skLineSegment(sketch, "E40.8.0.0", {"start": v(5.45, 54.71) * mm, "end": v(0.83, 54.71) * mm});
            skLineSegment(sketch, "E40.8.0.1", {"start": v(5.45, 59.33) * mm, "end": v(5.45, 54.71) * mm});
            skLineSegment(sketch, "E40.8.0.2", {"start": v(5.45, 59.33) * mm, "end": v(0.83, 59.33) * mm});
            skLineSegment(sketch, "E40.8.0.3", {"start": v(0.83, 59.33) * mm, "end": v(0.83, 54.71) * mm});
            skLineSegment(sketch, "E40.8.1.0", {"start": v(5.45, 42.01) * mm, "end": v(0.83, 42.01) * mm});
            skLineSegment(sketch, "E40.8.1.1", {"start": v(5.45, 46.63) * mm, "end": v(5.45, 42.01) * mm});
            skLineSegment(sketch, "E40.8.1.2", {"start": v(5.45, 46.63) * mm, "end": v(0.83, 46.63) * mm});
            skLineSegment(sketch, "E40.8.1.3", {"start": v(0.83, 46.63) * mm, "end": v(0.83, 42.01) * mm});
            skLineSegment(sketch, "E40.8.2.0", {"start": v(5.45, 29.31) * mm, "end": v(0.83, 29.31) * mm});
            skLineSegment(sketch, "E40.8.2.1", {"start": v(5.45, 33.93) * mm, "end": v(5.45, 29.31) * mm});
            skLineSegment(sketch, "E40.8.2.2", {"start": v(5.45, 33.93) * mm, "end": v(0.83, 33.93) * mm});
            skLineSegment(sketch, "E40.8.2.3", {"start": v(0.83, 33.93) * mm, "end": v(0.83, 29.31) * mm});
            skLineSegment(sketch, "E40.8.3.0", {"start": v(5.45, 16.61) * mm, "end": v(0.83, 16.61) * mm});
            skLineSegment(sketch, "E40.8.3.1", {"start": v(5.45, 21.23) * mm, "end": v(5.45, 16.61) * mm});
            skLineSegment(sketch, "E40.8.3.2", {"start": v(5.45, 21.23) * mm, "end": v(0.83, 21.23) * mm});
            skLineSegment(sketch, "E40.8.3.3", {"start": v(0.83, 21.23) * mm, "end": v(0.83, 16.61) * mm});
            skLineSegment(sketch, "E40.8.4.0", {"start": v(5.45, 3.91) * mm, "end": v(0.83, 3.91) * mm});
            skLineSegment(sketch, "E40.8.4.1", {"start": v(5.45, 8.53) * mm, "end": v(5.45, 3.91) * mm});
            skLineSegment(sketch, "E40.8.4.2", {"start": v(5.45, 8.53) * mm, "end": v(0.83, 8.53) * mm});
            skLineSegment(sketch, "E40.8.4.3", {"start": v(0.83, 8.53) * mm, "end": v(0.83, 3.91) * mm});
            skLineSegment(sketch, "E40.9.0.0", {"start": v(-7.25, 54.71) * mm, "end": v(-11.87, 54.71) * mm});
            skLineSegment(sketch, "E40.9.0.1", {"start": v(-7.25, 59.33) * mm, "end": v(-7.25, 54.71) * mm});
            skLineSegment(sketch, "E40.9.0.2", {"start": v(-7.25, 59.33) * mm, "end": v(-11.87, 59.33) * mm});
            skLineSegment(sketch, "E40.9.0.3", {"start": v(-11.87, 59.33) * mm, "end": v(-11.87, 54.71) * mm});
            skLineSegment(sketch, "E40.9.1.0", {"start": v(-7.25, 42.01) * mm, "end": v(-11.87, 42.01) * mm});
            skLineSegment(sketch, "E40.9.1.1", {"start": v(-7.25, 46.63) * mm, "end": v(-7.25, 42.01) * mm});
            skLineSegment(sketch, "E40.9.1.2", {"start": v(-7.25, 46.63) * mm, "end": v(-11.87, 46.63) * mm});
            skLineSegment(sketch, "E40.9.1.3", {"start": v(-11.87, 46.63) * mm, "end": v(-11.87, 42.01) * mm});
            skLineSegment(sketch, "E40.9.2.0", {"start": v(-7.25, 29.31) * mm, "end": v(-11.87, 29.31) * mm});
            skLineSegment(sketch, "E40.9.2.1", {"start": v(-7.25, 33.93) * mm, "end": v(-7.25, 29.31) * mm});
            skLineSegment(sketch, "E40.9.2.2", {"start": v(-7.25, 33.93) * mm, "end": v(-11.87, 33.93) * mm});
            skLineSegment(sketch, "E40.9.2.3", {"start": v(-11.87, 33.93) * mm, "end": v(-11.87, 29.31) * mm});
            skLineSegment(sketch, "E40.9.3.0", {"start": v(-7.25, 16.61) * mm, "end": v(-11.87, 16.61) * mm});
            skLineSegment(sketch, "E40.9.3.1", {"start": v(-7.25, 21.23) * mm, "end": v(-7.25, 16.61) * mm});
            skLineSegment(sketch, "E40.9.3.2", {"start": v(-7.25, 21.23) * mm, "end": v(-11.87, 21.23) * mm});
            skLineSegment(sketch, "E40.9.3.3", {"start": v(-11.87, 21.23) * mm, "end": v(-11.87, 16.61) * mm});
            skLineSegment(sketch, "E40.9.4.0", {"start": v(-7.25, 3.91) * mm, "end": v(-11.87, 3.91) * mm});
            skLineSegment(sketch, "E40.9.4.1", {"start": v(-7.25, 8.53) * mm, "end": v(-7.25, 3.91) * mm});
            skLineSegment(sketch, "E40.9.4.2", {"start": v(-7.25, 8.53) * mm, "end": v(-11.87, 8.53) * mm});
            skLineSegment(sketch, "E40.9.4.3", {"start": v(-11.87, 8.53) * mm, "end": v(-11.87, 3.91) * mm});
            skLineSegment(sketch, "E40.10.0.0", {"start": v(-19.95, 54.71) * mm, "end": v(-24.57, 54.71) * mm});
            skLineSegment(sketch, "E40.10.0.1", {"start": v(-19.95, 59.33) * mm, "end": v(-19.95, 54.71) * mm});
            skLineSegment(sketch, "E40.10.0.2", {"start": v(-19.95, 59.33) * mm, "end": v(-24.57, 59.33) * mm});
            skLineSegment(sketch, "E40.10.0.3", {"start": v(-24.57, 59.33) * mm, "end": v(-24.57, 54.71) * mm});
            skLineSegment(sketch, "E40.10.1.0", {"start": v(-19.95, 42.01) * mm, "end": v(-24.57, 42.01) * mm});
            skLineSegment(sketch, "E40.10.1.1", {"start": v(-19.95, 46.63) * mm, "end": v(-19.95, 42.01) * mm});
            skLineSegment(sketch, "E40.10.1.2", {"start": v(-19.95, 46.63) * mm, "end": v(-24.57, 46.63) * mm});
            skLineSegment(sketch, "E40.10.1.3", {"start": v(-24.57, 46.63) * mm, "end": v(-24.57, 42.01) * mm});
            skLineSegment(sketch, "E40.10.2.0", {"start": v(-19.95, 29.31) * mm, "end": v(-24.57, 29.31) * mm});
            skLineSegment(sketch, "E40.10.2.1", {"start": v(-19.95, 33.93) * mm, "end": v(-19.95, 29.31) * mm});
            skLineSegment(sketch, "E40.10.2.2", {"start": v(-19.95, 33.93) * mm, "end": v(-24.57, 33.93) * mm});
            skLineSegment(sketch, "E40.10.2.3", {"start": v(-24.57, 33.93) * mm, "end": v(-24.57, 29.31) * mm});
            skLineSegment(sketch, "E40.10.3.0", {"start": v(-19.95, 16.61) * mm, "end": v(-24.57, 16.61) * mm});
            skLineSegment(sketch, "E40.10.3.1", {"start": v(-19.95, 21.23) * mm, "end": v(-19.95, 16.61) * mm});
            skLineSegment(sketch, "E40.10.3.2", {"start": v(-19.95, 21.23) * mm, "end": v(-24.57, 21.23) * mm});
            skLineSegment(sketch, "E40.10.3.3", {"start": v(-24.57, 21.23) * mm, "end": v(-24.57, 16.61) * mm});
            skLineSegment(sketch, "E40.10.4.0", {"start": v(-19.95, 3.91) * mm, "end": v(-24.57, 3.91) * mm});
            skLineSegment(sketch, "E40.10.4.1", {"start": v(-19.95, 8.53) * mm, "end": v(-19.95, 3.91) * mm});
            skLineSegment(sketch, "E40.10.4.2", {"start": v(-19.95, 8.53) * mm, "end": v(-24.57, 8.53) * mm});
            skLineSegment(sketch, "E40.10.4.3", {"start": v(-24.57, 8.53) * mm, "end": v(-24.57, 3.91) * mm});
            skLineSegment(sketch, "E40.11.0.0", {"start": v(-32.65, 54.71) * mm, "end": v(-37.27, 54.71) * mm});
            skLineSegment(sketch, "E40.11.0.1", {"start": v(-32.65, 59.33) * mm, "end": v(-32.65, 54.71) * mm});
            skLineSegment(sketch, "E40.11.0.2", {"start": v(-32.65, 59.33) * mm, "end": v(-37.27, 59.33) * mm});
            skLineSegment(sketch, "E40.11.0.3", {"start": v(-37.27, 59.33) * mm, "end": v(-37.27, 54.71) * mm});
            skLineSegment(sketch, "E40.11.1.0", {"start": v(-32.65, 42.01) * mm, "end": v(-37.27, 42.01) * mm});
            skLineSegment(sketch, "E40.11.1.1", {"start": v(-32.65, 46.63) * mm, "end": v(-32.65, 42.01) * mm});
            skLineSegment(sketch, "E40.11.1.2", {"start": v(-32.65, 46.63) * mm, "end": v(-37.27, 46.63) * mm});
            skLineSegment(sketch, "E40.11.1.3", {"start": v(-37.27, 46.63) * mm, "end": v(-37.27, 42.01) * mm});
            skLineSegment(sketch, "E40.11.2.0", {"start": v(-32.65, 29.31) * mm, "end": v(-37.27, 29.31) * mm});
            skLineSegment(sketch, "E40.11.2.1", {"start": v(-32.65, 33.93) * mm, "end": v(-32.65, 29.31) * mm});
            skLineSegment(sketch, "E40.11.2.2", {"start": v(-32.65, 33.93) * mm, "end": v(-37.27, 33.93) * mm});
            skLineSegment(sketch, "E40.11.2.3", {"start": v(-37.27, 33.93) * mm, "end": v(-37.27, 29.31) * mm});
            skLineSegment(sketch, "E40.11.3.0", {"start": v(-32.65, 16.61) * mm, "end": v(-37.27, 16.61) * mm});
            skLineSegment(sketch, "E40.11.3.1", {"start": v(-32.65, 21.23) * mm, "end": v(-32.65, 16.61) * mm});
            skLineSegment(sketch, "E40.11.3.2", {"start": v(-32.65, 21.23) * mm, "end": v(-37.27, 21.23) * mm});
            skLineSegment(sketch, "E40.11.3.3", {"start": v(-37.27, 21.23) * mm, "end": v(-37.27, 16.61) * mm});
            skLineSegment(sketch, "E40.11.4.0", {"start": v(-32.65, 3.91) * mm, "end": v(-37.27, 3.91) * mm});
            skLineSegment(sketch, "E40.11.4.1", {"start": v(-32.65, 8.53) * mm, "end": v(-32.65, 3.91) * mm});
            skLineSegment(sketch, "E40.11.4.2", {"start": v(-32.65, 8.53) * mm, "end": v(-37.27, 8.53) * mm});
            skLineSegment(sketch, "E40.11.4.3", {"start": v(-37.27, 8.53) * mm, "end": v(-37.27, 3.91) * mm});
            skLineSegment(sketch, "E40.12.0.0", {"start": v(-45.35, 54.71) * mm, "end": v(-49.97, 54.71) * mm});
            skLineSegment(sketch, "E40.12.0.1", {"start": v(-45.35, 59.33) * mm, "end": v(-45.35, 54.71) * mm});
            skLineSegment(sketch, "E40.12.0.2", {"start": v(-45.35, 59.33) * mm, "end": v(-49.97, 59.33) * mm});
            skLineSegment(sketch, "E40.12.0.3", {"start": v(-49.97, 59.33) * mm, "end": v(-49.97, 54.71) * mm});
            skLineSegment(sketch, "E40.12.1.0", {"start": v(-45.35, 42.01) * mm, "end": v(-49.97, 42.01) * mm});
            skLineSegment(sketch, "E40.12.1.1", {"start": v(-45.35, 46.63) * mm, "end": v(-45.35, 42.01) * mm});
            skLineSegment(sketch, "E40.12.1.2", {"start": v(-45.35, 46.63) * mm, "end": v(-49.97, 46.63) * mm});
            skLineSegment(sketch, "E40.12.1.3", {"start": v(-49.97, 46.63) * mm, "end": v(-49.97, 42.01) * mm});
            skLineSegment(sketch, "E40.12.2.0", {"start": v(-45.35, 29.31) * mm, "end": v(-49.97, 29.31) * mm});
            skLineSegment(sketch, "E40.12.2.1", {"start": v(-45.35, 33.93) * mm, "end": v(-45.35, 29.31) * mm});
            skLineSegment(sketch, "E40.12.2.2", {"start": v(-45.35, 33.93) * mm, "end": v(-49.97, 33.93) * mm});
            skLineSegment(sketch, "E40.12.2.3", {"start": v(-49.97, 33.93) * mm, "end": v(-49.97, 29.31) * mm});
            skLineSegment(sketch, "E40.12.3.0", {"start": v(-45.35, 16.61) * mm, "end": v(-49.97, 16.61) * mm});
            skLineSegment(sketch, "E40.12.3.1", {"start": v(-45.35, 21.23) * mm, "end": v(-45.35, 16.61) * mm});
            skLineSegment(sketch, "E40.12.3.2", {"start": v(-45.35, 21.23) * mm, "end": v(-49.97, 21.23) * mm});
            skLineSegment(sketch, "E40.12.3.3", {"start": v(-49.97, 21.23) * mm, "end": v(-49.97, 16.61) * mm});
            skLineSegment(sketch, "E40.12.4.0", {"start": v(-45.35, 3.91) * mm, "end": v(-49.97, 3.91) * mm});
            skLineSegment(sketch, "E40.12.4.1", {"start": v(-45.35, 8.53) * mm, "end": v(-45.35, 3.91) * mm});
            skLineSegment(sketch, "E40.12.4.2", {"start": v(-45.35, 8.53) * mm, "end": v(-49.97, 8.53) * mm});
            skLineSegment(sketch, "E40.12.4.3", {"start": v(-49.97, 8.53) * mm, "end": v(-49.97, 3.91) * mm});
            skLineSegment(sketch, "E40.13.0.0", {"start": v(-58.05, 54.71) * mm, "end": v(-62.67, 54.71) * mm});
            skLineSegment(sketch, "E40.13.0.1", {"start": v(-58.05, 59.33) * mm, "end": v(-58.05, 54.71) * mm});
            skLineSegment(sketch, "E40.13.0.2", {"start": v(-58.05, 59.33) * mm, "end": v(-62.67, 59.33) * mm});
            skLineSegment(sketch, "E40.13.0.3", {"start": v(-62.67, 59.33) * mm, "end": v(-62.67, 54.71) * mm});
            skLineSegment(sketch, "E40.13.1.0", {"start": v(-58.05, 42.01) * mm, "end": v(-62.67, 42.01) * mm});
            skLineSegment(sketch, "E40.13.1.1", {"start": v(-58.05, 46.63) * mm, "end": v(-58.05, 42.01) * mm});
            skLineSegment(sketch, "E40.13.1.2", {"start": v(-58.05, 46.63) * mm, "end": v(-62.67, 46.63) * mm});
            skLineSegment(sketch, "E40.13.1.3", {"start": v(-62.67, 46.63) * mm, "end": v(-62.67, 42.01) * mm});
            skLineSegment(sketch, "E40.13.2.0", {"start": v(-58.05, 29.31) * mm, "end": v(-62.67, 29.31) * mm});
            skLineSegment(sketch, "E40.13.2.1", {"start": v(-58.05, 33.93) * mm, "end": v(-58.05, 29.31) * mm});
            skLineSegment(sketch, "E40.13.2.2", {"start": v(-58.05, 33.93) * mm, "end": v(-62.67, 33.93) * mm});
            skLineSegment(sketch, "E40.13.2.3", {"start": v(-62.67, 33.93) * mm, "end": v(-62.67, 29.31) * mm});
            skLineSegment(sketch, "E40.13.3.0", {"start": v(-58.05, 16.61) * mm, "end": v(-62.67, 16.61) * mm});
            skLineSegment(sketch, "E40.13.3.1", {"start": v(-58.05, 21.23) * mm, "end": v(-58.05, 16.61) * mm});
            skLineSegment(sketch, "E40.13.3.2", {"start": v(-58.05, 21.23) * mm, "end": v(-62.67, 21.23) * mm});
            skLineSegment(sketch, "E40.13.3.3", {"start": v(-62.67, 21.23) * mm, "end": v(-62.67, 16.61) * mm});
            skLineSegment(sketch, "E40.13.4.0", {"start": v(-58.05, 3.91) * mm, "end": v(-62.67, 3.91) * mm});
            skLineSegment(sketch, "E40.13.4.1", {"start": v(-58.05, 8.53) * mm, "end": v(-58.05, 3.91) * mm});
            skLineSegment(sketch, "E40.13.4.2", {"start": v(-58.05, 8.53) * mm, "end": v(-62.67, 8.53) * mm});
            skLineSegment(sketch, "E40.13.4.3", {"start": v(-62.67, 8.53) * mm, "end": v(-62.67, 3.91) * mm});
            skLineSegment(sketch, "E40.direction1", {"start": v(102.43, 54.71) * mm, "end": v(89.73, 54.71) * mm, "construction": true});
            skLineSegment(sketch, "E40.direction2", {"start": v(102.43, 54.71) * mm, "end": v(102.43, 42.01) * mm, "construction": true});
            skLineSegment(sketch, "E41.0.14.0", {"start": v(-70.75, 54.71) * mm, "end": v(-75.37, 54.71) * mm});
            skLineSegment(sketch, "E41.3.14.0", {"start": v(-70.75, 59.33) * mm, "end": v(-70.75, 54.71) * mm});
            skLineSegment(sketch, "E41.6.14.0", {"start": v(-70.75, 59.33) * mm, "end": v(-75.37, 59.33) * mm});
            skLineSegment(sketch, "E41.9.14.0", {"start": v(-75.37, 59.33) * mm, "end": v(-75.37, 54.71) * mm});
            skLineSegment(sketch, "E41.0.14.1", {"start": v(-70.75, 42.01) * mm, "end": v(-75.37, 42.01) * mm});
            skLineSegment(sketch, "E41.3.14.1", {"start": v(-70.75, 46.63) * mm, "end": v(-70.75, 42.01) * mm});
            skLineSegment(sketch, "E41.6.14.1", {"start": v(-70.75, 46.63) * mm, "end": v(-75.37, 46.63) * mm});
            skLineSegment(sketch, "E41.9.14.1", {"start": v(-75.37, 46.63) * mm, "end": v(-75.37, 42.01) * mm});
            skLineSegment(sketch, "E41.0.14.2", {"start": v(-70.75, 29.31) * mm, "end": v(-75.37, 29.31) * mm});
            skLineSegment(sketch, "E41.3.14.2", {"start": v(-70.75, 33.93) * mm, "end": v(-70.75, 29.31) * mm});
            skLineSegment(sketch, "E41.6.14.2", {"start": v(-70.75, 33.93) * mm, "end": v(-75.37, 33.93) * mm});
            skLineSegment(sketch, "E41.9.14.2", {"start": v(-75.37, 33.93) * mm, "end": v(-75.37, 29.31) * mm});
            skLineSegment(sketch, "E41.0.14.3", {"start": v(-70.75, 16.61) * mm, "end": v(-75.37, 16.61) * mm});
            skLineSegment(sketch, "E41.3.14.3", {"start": v(-70.75, 21.23) * mm, "end": v(-70.75, 16.61) * mm});
            skLineSegment(sketch, "E41.6.14.3", {"start": v(-70.75, 21.23) * mm, "end": v(-75.37, 21.23) * mm});
            skLineSegment(sketch, "E41.9.14.3", {"start": v(-75.37, 21.23) * mm, "end": v(-75.37, 16.61) * mm});
            skLineSegment(sketch, "E41.0.14.4", {"start": v(-70.75, 3.91) * mm, "end": v(-75.37, 3.91) * mm});
            skLineSegment(sketch, "E41.3.14.4", {"start": v(-70.75, 8.53) * mm, "end": v(-70.75, 3.91) * mm});
            skLineSegment(sketch, "E41.6.14.4", {"start": v(-70.75, 8.53) * mm, "end": v(-75.37, 8.53) * mm});
            skLineSegment(sketch, "E41.9.14.4", {"start": v(-75.37, 8.53) * mm, "end": v(-75.37, 3.91) * mm});
            skLineSegment(sketch, "E41.0.15.0", {"start": v(-83.45, 54.71) * mm, "end": v(-88.07, 54.71) * mm});
            skLineSegment(sketch, "E41.3.15.0", {"start": v(-83.45, 59.33) * mm, "end": v(-83.45, 54.71) * mm});
            skLineSegment(sketch, "E41.6.15.0", {"start": v(-83.45, 59.33) * mm, "end": v(-88.07, 59.33) * mm});
            skLineSegment(sketch, "E41.9.15.0", {"start": v(-88.07, 59.33) * mm, "end": v(-88.07, 54.71) * mm});
            skLineSegment(sketch, "E41.0.15.1", {"start": v(-83.45, 42.01) * mm, "end": v(-88.07, 42.01) * mm});
            skLineSegment(sketch, "E41.3.15.1", {"start": v(-83.45, 46.63) * mm, "end": v(-83.45, 42.01) * mm});
            skLineSegment(sketch, "E41.6.15.1", {"start": v(-83.45, 46.63) * mm, "end": v(-88.07, 46.63) * mm});
            skLineSegment(sketch, "E41.9.15.1", {"start": v(-88.07, 46.63) * mm, "end": v(-88.07, 42.01) * mm});
            skLineSegment(sketch, "E41.0.15.2", {"start": v(-83.45, 29.31) * mm, "end": v(-88.07, 29.31) * mm});
            skLineSegment(sketch, "E41.3.15.2", {"start": v(-83.45, 33.93) * mm, "end": v(-83.45, 29.31) * mm});
            skLineSegment(sketch, "E41.6.15.2", {"start": v(-83.45, 33.93) * mm, "end": v(-88.07, 33.93) * mm});
            skLineSegment(sketch, "E41.9.15.2", {"start": v(-88.07, 33.93) * mm, "end": v(-88.07, 29.31) * mm});
            skLineSegment(sketch, "E41.0.15.3", {"start": v(-83.45, 16.61) * mm, "end": v(-88.07, 16.61) * mm});
            skLineSegment(sketch, "E41.3.15.3", {"start": v(-83.45, 21.23) * mm, "end": v(-83.45, 16.61) * mm});
            skLineSegment(sketch, "E41.6.15.3", {"start": v(-83.45, 21.23) * mm, "end": v(-88.07, 21.23) * mm});
            skLineSegment(sketch, "E41.9.15.3", {"start": v(-88.07, 21.23) * mm, "end": v(-88.07, 16.61) * mm});
            skLineSegment(sketch, "E41.0.15.4", {"start": v(-83.45, 3.91) * mm, "end": v(-88.07, 3.91) * mm});
            skLineSegment(sketch, "E41.3.15.4", {"start": v(-83.45, 8.53) * mm, "end": v(-83.45, 3.91) * mm});
            skLineSegment(sketch, "E41.6.15.4", {"start": v(-83.45, 8.53) * mm, "end": v(-88.07, 8.53) * mm});
            skLineSegment(sketch, "E41.9.15.4", {"start": v(-88.07, 8.53) * mm, "end": v(-88.07, 3.91) * mm});
            skSolve(sketch);
        }
        {
            var Q0;
            Q0=makeQuery(id+"F1.imprint","IMPRINT",FACE,{"disambiguationData":[TD([[makeQuery(id+"F1.imprint","IMPRINT",EDGE,{"derivedFrom":sQuery(id+"F1.wireOp",EDGE,"E35")}),1.0]])]});
            var Q1;
            {var subQ1=sQuery(id+"F1.wireOp",EDGE,"8ea1a07a-7ca9-4907-9e18-5108a9660366");Q1=makeQuery(id+"F1.imprint","IMPRINT",FACE,{"disambiguationData":[TD([[makeQuery(id+"F1.imprint","IMPRINT",EDGE,{"derivedFrom":subQ1}),1.0]])]});}
            extrude(context, id + "F2", {"entities" : qUnion([Q0, Q1]), "depth" : 2.54 * mm});
        }
        {
            var Q0;
            Q0=makeQuery(id+"F0.imprint","IMPRINT",FACE,{"disambiguationData":[TD([[makeQuery(id+"F0.imprint","IMPRINT",EDGE,{"derivedFrom":sQuery(id+"F0.wireOp",EDGE,"E0.bottom")}),-1.0]])]});
            extrude(context, id + "F3", {"entities" : qUnion([Q0]), "oppositeDirection" : true, "depth" : 2.54 * mm});
        }
    });
